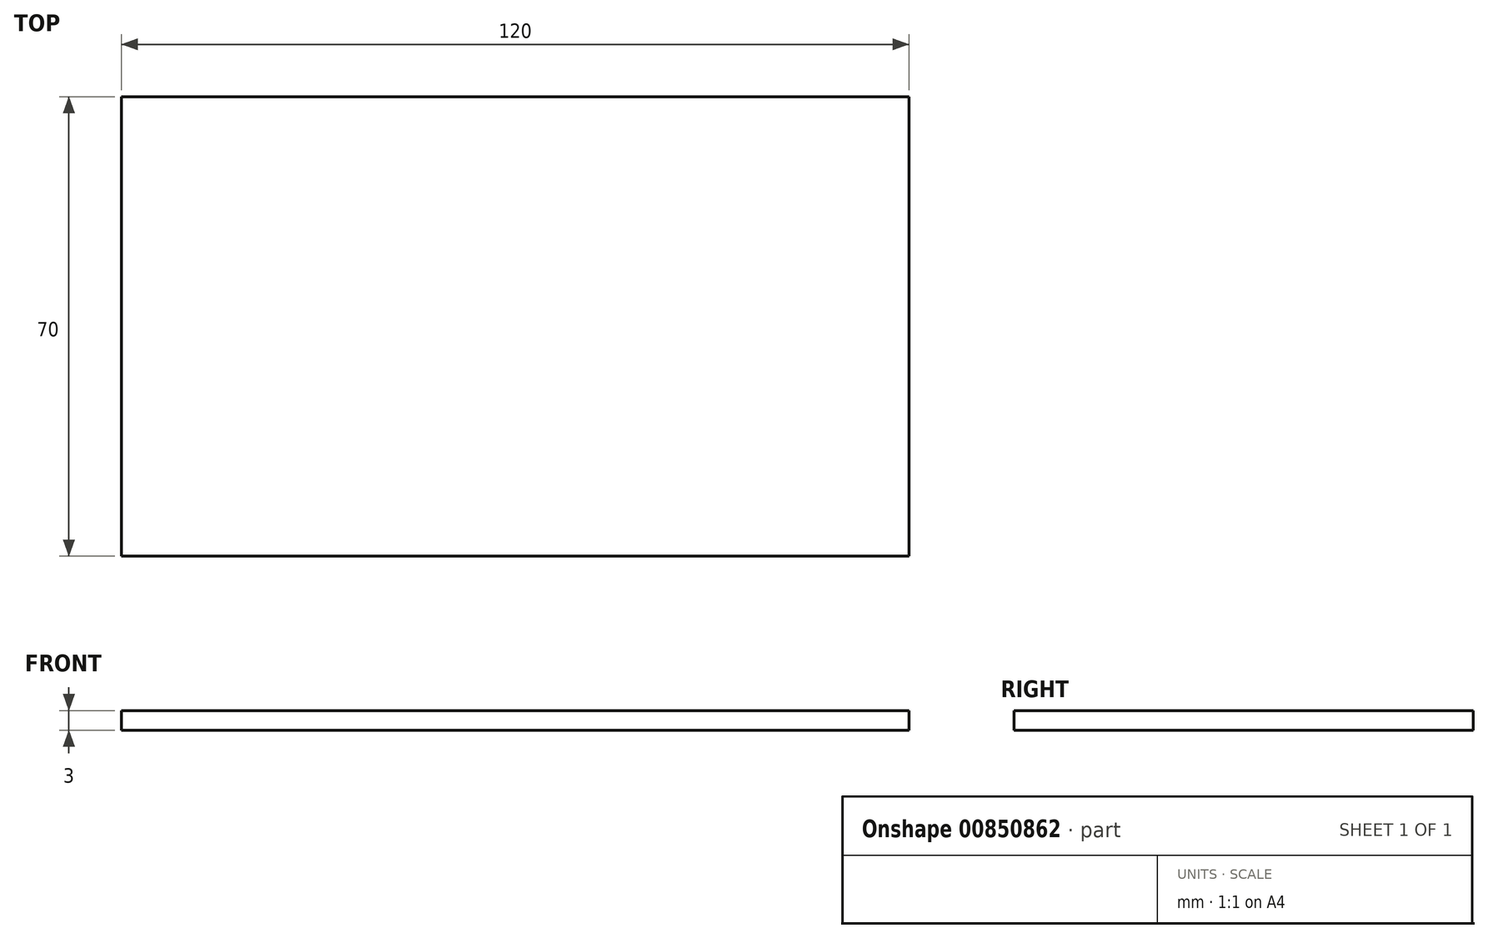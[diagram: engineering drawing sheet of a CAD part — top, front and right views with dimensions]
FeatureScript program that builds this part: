
annotation { "Feature Type Name" : "Feature", "Feature Type Description" : "" }
export const myFeature = defineFeature(function(context is Context, id is Id, definition is map)
    precondition{}
    {
        {
            var Q0;
            Q0=qCreatedBy(makeId("Top.planeOp"),FACE);
            var sketch = newSketch(context, id + "F0", { "sketchPlane" : qUnion([Q0])});
            skLineSegment(sketch, "E0.bottom", {"start": v(60, 35) * mm, "end": v(-60, 35) * mm});
            skLineSegment(sketch, "E0.top", {"start": v(60, -35) * mm, "end": v(-60, -35) * mm});
            skLineSegment(sketch, "E0.left", {"start": v(60, 35) * mm, "end": v(60, -35) * mm});
            skLineSegment(sketch, "E0.right", {"start": v(-60, 35) * mm, "end": v(-60, -35) * mm});
            skPoint(sketch, "E0.middle", {"position": v(0, 0) * mm});
            skSolve(sketch);
        }
        {
            var Q0;
            Q0 = qSketchRegion(id + "F0", true);
            extrude(context, id + "F1", {"entities" : qUnion([Q0]), "depth" : 3 * mm, "offsetDistance" : 25 * mm});
        }
    });
